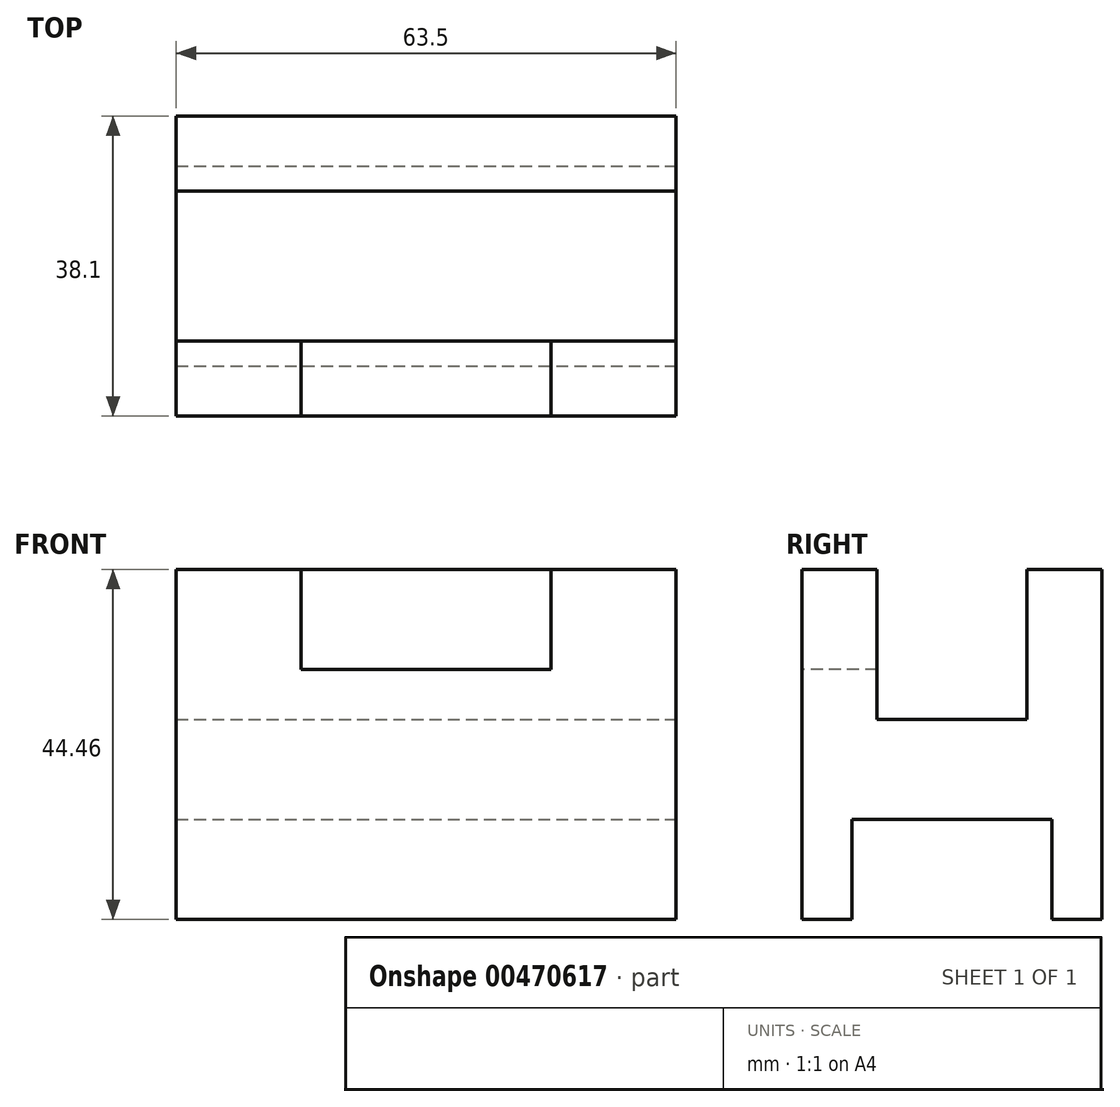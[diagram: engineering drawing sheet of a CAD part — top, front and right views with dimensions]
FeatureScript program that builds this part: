
annotation { "Feature Type Name" : "Feature", "Feature Type Description" : "" }
export const myFeature = defineFeature(function(context is Context, id is Id, definition is map)
    precondition{}
    {
        {
            var Q0;
            Q0=qCreatedBy(makeId("Front.planeOp"),FACE);
            var sketch = newSketch(context, id + "F0", { "sketchPlane" : qUnion([Q0])});
            skLineSegment(sketch, "E0.bottom", {"start": v(31.75, -22.23) * mm, "end": v(-31.75, -22.23) * mm});
            skLineSegment(sketch, "E0.top", {"start": v(31.75, 22.23) * mm, "end": v(-31.75, 22.22) * mm});
            skLineSegment(sketch, "E0.left", {"start": v(31.75, -22.23) * mm, "end": v(31.75, 22.23) * mm});
            skLineSegment(sketch, "E0.right", {"start": v(-31.75, -22.23) * mm, "end": v(-31.75, 22.22) * mm});
            skPoint(sketch, "E0.middle", {"position": v(0, 0) * mm});
            skSolve(sketch);
        }
        {
            var Q0;
            Q0 = qSketchRegion(id + "F0", true);
            extrude(context, id + "F1", {"entities" : qUnion([Q0]), "depth" : 38.1 * mm});
        }
        {
            var Q0;
            Q0=makeQuery(id+"F1.opExtrude","SWEPT_FACE",FACE,{"disambiguationData":[OSD([sQuery(id+"F0.wireOp",EDGE,"E0.left")])]});
            var sketch = newSketch(context, id + "F2", { "sketchPlane" : qUnion([Q0])});
            skLineSegment(sketch, "E1.bottom", {"start": v(-31.75, -22.23) * mm, "end": v(-6.35, -22.23) * mm});
            skLineSegment(sketch, "E1.top", {"start": v(-31.75, -9.53) * mm, "end": v(-6.35, -9.53) * mm});
            skLineSegment(sketch, "E1.left", {"start": v(-31.75, -22.23) * mm, "end": v(-31.75, -9.53) * mm});
            skLineSegment(sketch, "E1.right", {"start": v(-6.35, -22.23) * mm, "end": v(-6.35, -9.53) * mm});
            skLineSegment(sketch, "E2.bottom", {"start": v(-28.58, 22.23) * mm, "end": v(-9.52, 22.23) * mm});
            skLineSegment(sketch, "E2.top", {"start": v(-28.58, 3.18) * mm, "end": v(-9.53, 3.18) * mm});
            skLineSegment(sketch, "E2.left", {"start": v(-28.58, 22.23) * mm, "end": v(-28.58, 3.18) * mm});
            skLineSegment(sketch, "E2.right", {"start": v(-9.53, 22.23) * mm, "end": v(-9.53, 3.18) * mm});
            skSolve(sketch);
        }
        {
            var Q0;
            Q0 = qSketchRegion(id + "F2", true);
            extrude(context, id + "F3", {"entities" : qUnion([Q0]), "operationType" : NewBodyOperationType.REMOVE, "endBound" : BoundingType.THROUGH_ALL, "oppositeDirection" : true, "depth" : 25.4 * mm});
        }
        {
            var Q0;
            Q0=makeQuery(id+"F1.opExtrude","CAP_FACE",FACE,{"disambiguationData":[OSD([sQuery(id+"F0.wireOp",EDGE,"E0.bottom"),sQuery(id+"F0.wireOp",EDGE,"E0.top"),sQuery(id+"F0.wireOp",EDGE,"E0.left"),sQuery(id+"F0.wireOp",EDGE,"E0.right")])],"isStart":false});
            var sketch = newSketch(context, id + "F4", { "sketchPlane" : qUnion([Q0])});
            skLineSegment(sketch, "E3.bottom", {"start": v(-15.88, 22.22) * mm, "end": v(15.87, 22.22) * mm});
            skLineSegment(sketch, "E3.top", {"start": v(-15.88, 9.53) * mm, "end": v(15.87, 9.53) * mm});
            skLineSegment(sketch, "E3.left", {"start": v(-15.88, 22.23) * mm, "end": v(-15.88, 9.53) * mm});
            skLineSegment(sketch, "E3.right", {"start": v(15.87, 22.23) * mm, "end": v(15.87, 9.53) * mm});
            skSolve(sketch);
        }
        {
            var Q0;
            Q0 = qSketchRegion(id + "F4", true);
            extrude(context, id + "F5", {"entities" : qUnion([Q0]), "operationType" : NewBodyOperationType.REMOVE, "oppositeDirection" : true, "depth" : 9.52 * mm});
        }
    });
